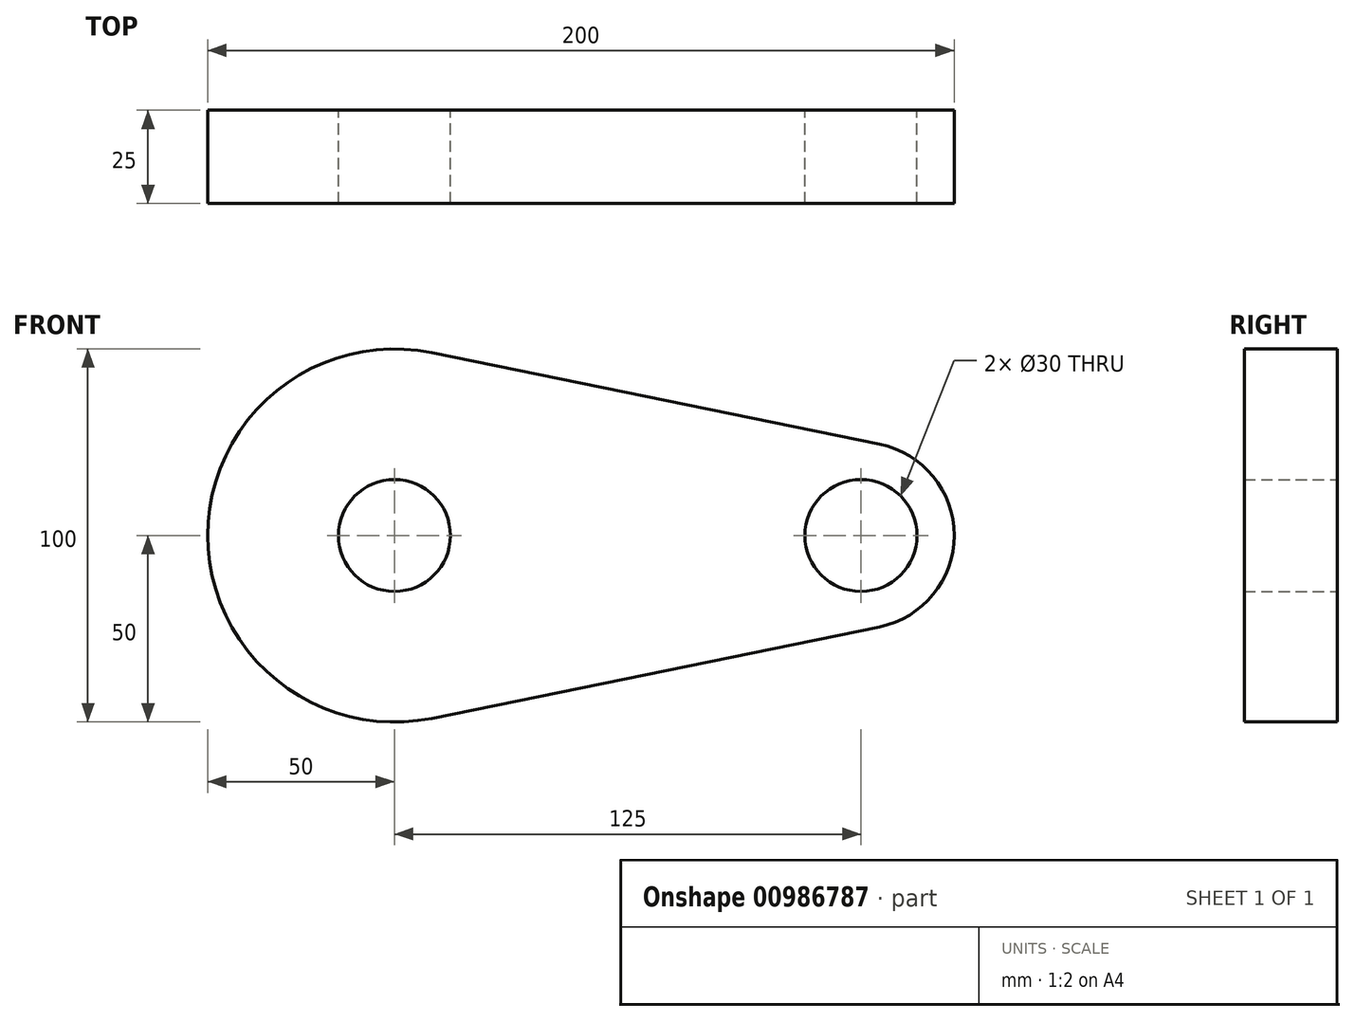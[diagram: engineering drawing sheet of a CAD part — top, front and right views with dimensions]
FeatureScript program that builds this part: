
annotation { "Feature Type Name" : "Feature", "Feature Type Description" : "" }
export const myFeature = defineFeature(function(context is Context, id is Id, definition is map)
    precondition{}
    {
        {
            var Q0;
            Q0=qCreatedBy(makeId("Front.planeOp"),FACE);
            var sketch = newSketch(context, id + "F0", { "sketchPlane" : qUnion([Q0])});
            skCircle(sketch, "E0", {"center": v(0, 0) * mm, "radius": 50 * mm});
            skCircle(sketch, "E1", {"center": v(125, 0) * mm, "radius": 25 * mm});
            skLineSegment(sketch, "E2", {"start": v(10, 48.99) * mm, "end": v(130, 24.5) * mm});
            skLineSegment(sketch, "E3", {"start": v(10, -48.99) * mm, "end": v(130, -24.5) * mm});
            skCircle(sketch, "E4", {"center": v(0, 0) * mm, "radius": 15 * mm});
            skCircle(sketch, "E5", {"center": v(125, 0) * mm, "radius": 15 * mm});
            skSolve(sketch);
        }
        {
            var Q0;
            Q0 = qSketchRegion(id + "F0", true);
            extrude(context, id + "F1", {"entities" : qUnion([Q0]), "depth" : 25 * mm, "offsetDistance" : 25 * mm});
        }
    });
